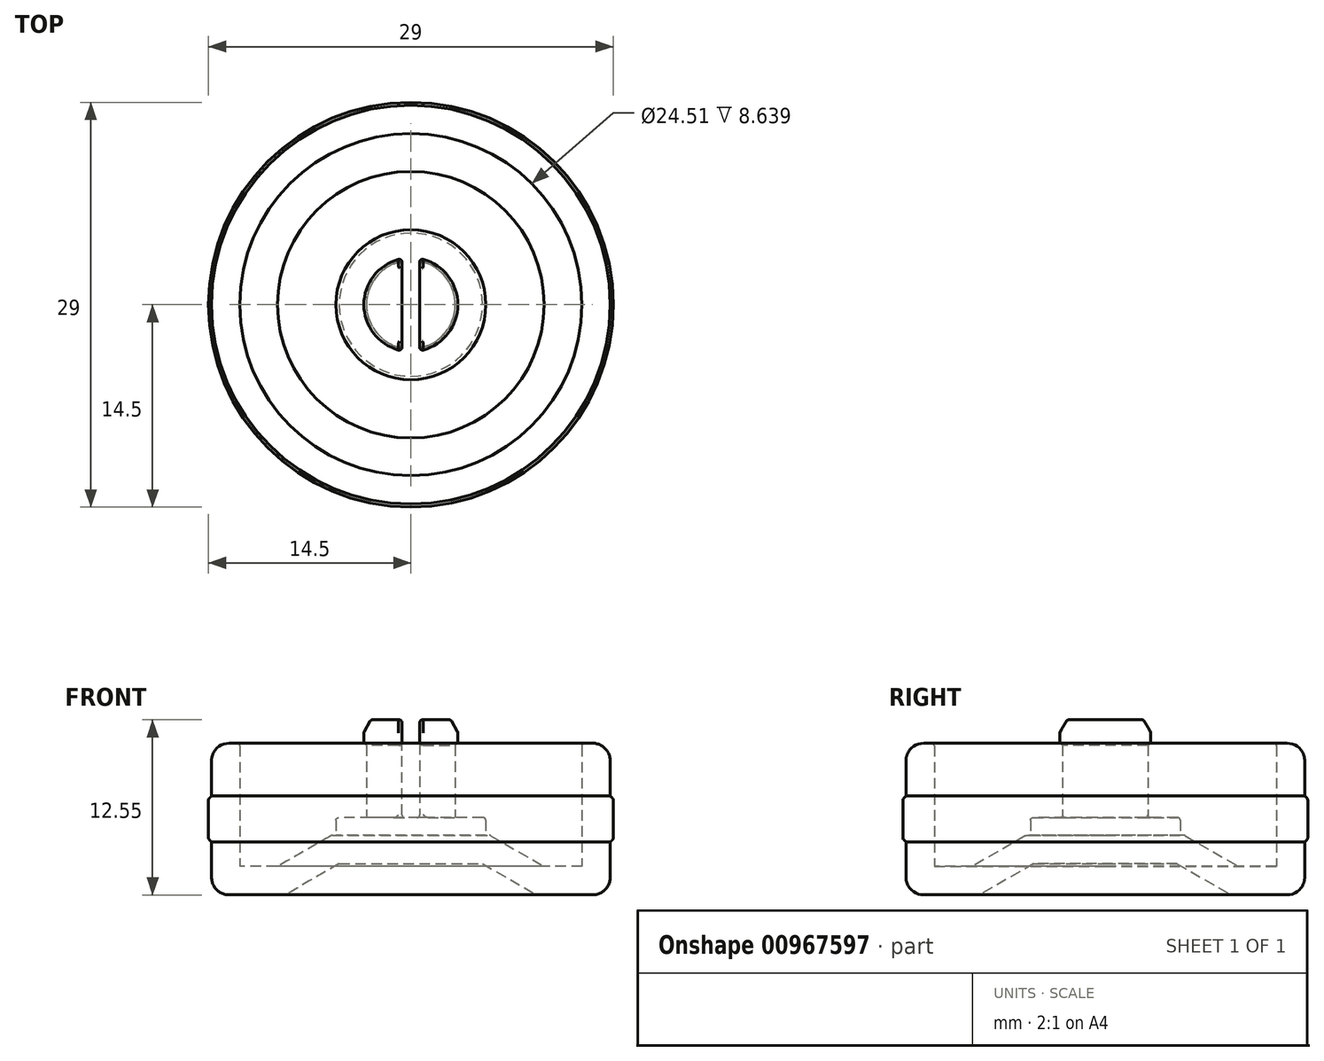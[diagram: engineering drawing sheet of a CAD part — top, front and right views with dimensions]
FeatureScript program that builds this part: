
annotation { "Feature Type Name" : "Feature", "Feature Type Description" : "" }
export const myFeature = defineFeature(function(context is Context, id is Id, definition is map)
    precondition{}
    {
        {
            var Q0;
            Q0=qCreatedBy(makeId("Top.planeOp"),FACE);
            var sketch = newSketch(context, id + "F0", { "sketchPlane" : qUnion([Q0])});
            skCircle(sketch, "E0", {"center": v(0, 0) * mm, "radius": 14.29 * mm});
            skSolve(sketch);
        }
        {
            var Q0;
            Q0 = qSketchRegion(id + "F0", true);
            extrude(context, id + "F1", {"entities" : qUnion([Q0]), "endBound" : BoundingType.SYMMETRIC, "depth" : 10.87 * mm, "offsetDistance" : 25.4 * mm});
        }
        {
            var Q0;
            Q0=qCreatedBy(makeId("Top.planeOp"),FACE);
            var sketch = newSketch(context, id + "F2", { "sketchPlane" : qUnion([Q0])});
            skCircle(sketch, "E1", {"center": v(0, 0) * mm, "radius": 14.5 * mm});
            skSolve(sketch);
        }
        {
            var Q0;
            Q0 = qSketchRegion(id + "F2", true);
            extrude(context, id + "F3", {"entities" : qUnion([Q0]), "operationType" : NewBodyOperationType.ADD, "endBound" : BoundingType.SYMMETRIC, "depth" : 3.38 * mm, "offsetDistance" : 25.4 * mm});
        }
        {
            var Q0;
            Q0=makeQuery(id+"F1.opExtrude","CAP_FACE",FACE,{"disambiguationData":[OSD([sQuery(id+"F0.wireOp",EDGE,"E0")])],"isStart":true});
            var sketch = newSketch(context, id + "F4", { "sketchPlane" : qUnion([Q0])});
            skCircle(sketch, "E2", {"center": v(0, 0) * mm, "radius": 9 * mm});
            skSolve(sketch);
        }
        {
            var Q0;
            Q0 = qSketchRegion(id + "F4", true);
            extrude(context, id + "F5", {"entities" : qUnion([Q0]), "operationType" : NewBodyOperationType.REMOVE, "oppositeDirection" : true, "depth" : 2.24 * mm, "offsetDistance" : 25.4 * mm});
        }
        {
            var Q0;
            Q0=makeQuery(id+"F5.boolean.opBoolean","COPY",EDGE,{"derivedFrom":makeQuery(id+"F5.opExtrude","CAP_EDGE",EDGE,{"disambiguationData":[OSD([sQuery(id+"F4.wireOp",EDGE,"E2")])],"isStart":false})});
            chamfer(context, id + "F6", {"entities" : qUnion([Q0]), "chamferType" : ChamferType.OFFSET_ANGLE, "width" : 2.24 * mm, "oppositeDirection" : true, "angle" : 60 * degree, "tangentPropagation" : true});
        }
        {
            var Q0;
            Q0=makeQuery(id+"F1.opExtrude","CAP_EDGE",EDGE,{"disambiguationData":[OSD([sQuery(id+"F0.wireOp",EDGE,"E0")])],"isStart":true});
            var Q1;
            Q1=makeQuery(id+"F1.opExtrude","CAP_EDGE",EDGE,{"disambiguationData":[OSD([sQuery(id+"F0.wireOp",EDGE,"E0")])],"isStart":false});
            fillet(context, id + "F7", {"entities" : qUnion([Q0, Q1]), "radius" : 1.27 * mm, "tangentPropagation" : true, "allowEdgeOverflow" : false});
        }
        {
            var Q0;
            Q0=makeQuery(id+"F1.opExtrude","CAP_FACE",FACE,{"disambiguationData":[OSD([sQuery(id+"F0.wireOp",EDGE,"E0")])],"isStart":false});
            shell(context, id + "F8", {"entities" : qUnion([Q0]), "thickness" : 2.03 * mm});
        }
        {
            var Q0;
            {var subQ0=sQuery(id+"F4.wireOp",EDGE,"E2");Q0=makeQuery(id+"F8.opShell","OFFSET_FACE",FACE,{"disambiguationData":[OSD([subQ0]),TDD([makeQuery(id+"F5.boolean.opBoolean","COPY",FACE,{"derivedFrom":makeQuery(id+"F5.opExtrude","CAP_FACE",FACE,{"disambiguationData":[OSD([subQ0])],"isStart":false})})])]});}
            var sketch = newSketch(context, id + "F9", { "sketchPlane" : qUnion([Q0])});
            skCircle(sketch, "E3", {"center": v(0, 0) * mm, "radius": 5.37 * mm});
            skSolve(sketch);
        }
        {
            var Q0;
            Q0 = qSketchRegion(id + "F9", true);
            extrude(context, id + "F10", {"entities" : qUnion([Q0]), "operationType" : NewBodyOperationType.ADD, "depth" : 1.27 * mm, "offsetDistance" : 25.4 * mm});
        }
        {
            var Q0;
            Q0=makeQuery(id+"F10.opExtrude","CAP_FACE",FACE,{"disambiguationData":[OSD([sQuery(id+"F9.wireOp",EDGE,"E3")])],"isStart":false});
            var sketch = newSketch(context, id + "F11", { "sketchPlane" : qUnion([Q0])});
            skCircle(sketch, "E4", {"center": v(0, 0) * mm, "radius": 3.18 * mm});
            skSolve(sketch);
        }
        {
            var Q0;
            Q0 = qSketchRegion(id + "F11", true);
            extrude(context, id + "F12", {"entities" : qUnion([Q0]), "operationType" : NewBodyOperationType.ADD, "depth" : 7 * mm, "offsetDistance" : 25.4 * mm});
        }
        {
            var Q0;
            Q0=makeQuery(id+"F12.opExtrude","CAP_FACE",FACE,{"disambiguationData":[OSD([sQuery(id+"F11.wireOp",EDGE,"E4")])],"isStart":false});
            var sketch = newSketch(context, id + "F13", { "sketchPlane" : qUnion([Q0])});
            skCircle(sketch, "E5", {"center": v(0, 0) * mm, "radius": 3.37 * mm});
            skSolve(sketch);
        }
        {
            var Q0;
            Q0 = qSketchRegion(id + "F13", true);
            extrude(context, id + "F14", {"entities" : qUnion([Q0]), "operationType" : NewBodyOperationType.ADD, "oppositeDirection" : true, "depth" : 1.9 * mm, "offsetDistance" : 25.4 * mm});
        }
        {
            var Q0;
            Q0=makeQuery(id+"F14.opExtrude","CAP_EDGE",EDGE,{"disambiguationData":[OSD([sQuery(id+"F13.wireOp",EDGE,"E5")])],"isStart":true});
            chamfer(context, id + "F15", {"entities" : qUnion([Q0]), "chamferType" : ChamferType.OFFSET_ANGLE, "width" : 0.5 * mm, "oppositeDirection" : false, "angle" : 60 * degree, "tangentPropagation" : true});
        }
        {
            var Q0;
            Q0=makeQuery(id+"F3.opExtrude","CAP_EDGE",EDGE,{"disambiguationData":[OSD([sQuery(id+"F2.wireOp",EDGE,"E1")])],"isStart":false});
            var Q1;
            Q1=makeQuery(id+"F3.opExtrude","CAP_EDGE",EDGE,{"disambiguationData":[OSD([sQuery(id+"F2.wireOp",EDGE,"E1")])],"isStart":true});
            chamfer(context, id + "F16", {"entities" : qUnion([Q0, Q1]), "width" : 0.25 * mm, "tangentPropagation" : true});
        }
        {
            var Q0;
            Q0=makeQuery(id+"F14.opExtrude","CAP_EDGE",EDGE,{"disambiguationData":[OSD([sQuery(id+"F13.wireOp",EDGE,"E5")])],"isStart":false});
            chamfer(context, id + "F17", {"entities" : qUnion([Q0]), "width" : 0.25 * mm, "tangentPropagation" : true});
        }
        {
            var Q0;
            Q0=makeQuery(id+"F14.boolean.opBoolean","MERGE",FACE,{"derivedFrom":[makeQuery(id+"F12.opExtrude","CAP_FACE",FACE,{"disambiguationData":[OSD([sQuery(id+"F11.wireOp",EDGE,"E4")])],"isStart":false}),makeQuery(id+"F14.opExtrude","CAP_FACE",FACE,{"disambiguationData":[OSD([sQuery(id+"F13.wireOp",EDGE,"E5")])],"isStart":true})]});
            var sketch = newSketch(context, id + "F18", { "sketchPlane" : qUnion([Q0])});
            skLineSegment(sketch, "E6", {"start": v(0, -3.37) * mm, "end": v(0, 3.37) * mm, "construction": true});
            skLineSegment(sketch, "E7.bottom", {"start": v(0.64, -3.37) * mm, "end": v(-0.64, -3.37) * mm});
            skLineSegment(sketch, "E7.top", {"start": v(0.64, 3.37) * mm, "end": v(-0.64, 3.37) * mm});
            skLineSegment(sketch, "E7.left", {"start": v(0.63, -3.37) * mm, "end": v(0.64, 3.37) * mm});
            skLineSegment(sketch, "E7.right", {"start": v(-0.64, -3.37) * mm, "end": v(-0.64, 3.37) * mm});
            skSolve(sketch);
        }
        {
            var Q0;
            Q0 = qSketchRegion(id + "F18", true);
            var Q1;
            Q1=makeQuery(id+"F10.opExtrude","CAP_FACE",FACE,{"disambiguationData":[OSD([sQuery(id+"F9.wireOp",EDGE,"E3")])],"isStart":false});
            extrude(context, id + "F19", {"entities" : qUnion([Q0]), "operationType" : NewBodyOperationType.REMOVE, "endBound" : BoundingType.UP_TO_SURFACE, "oppositeDirection" : true, "depth" : 25.4 * mm, "endBoundEntityFace" : qUnion([Q1]), "offsetDistance" : 25.4 * mm});
        }
        {
            var Q0;
            Q0=makeQuery(id+"F19.boolean.opBoolean","COPY",FACE,{"derivedFrom":makeQuery(id+"F19.opExtrude","SWEPT_FACE",FACE,{"disambiguationData":[OSD([sQuery(id+"F18.wireOp",EDGE,"E7.left")])]})});
            var Q1;
            Q1=makeQuery(id+"F19.boolean.opBoolean","COPY",FACE,{"derivedFrom":makeQuery(id+"F19.opExtrude","SWEPT_FACE",FACE,{"disambiguationData":[OSD([sQuery(id+"F18.wireOp",EDGE,"E7.right")])]})});
            var Q2;
            {var subQ0=makeQuery(id+"F12.opExtrude","CAP_FACE",FACE,{"disambiguationData":[OSD([sQuery(id+"F11.wireOp",EDGE,"E4")])],"isStart":false});var subQ1=sQuery(id+"F13.wireOp",EDGE,"E5");var subQ2=makeQuery(id+"F14.opExtrude","CAP_FACE",FACE,{"disambiguationData":[OSD([subQ1])],"isStart":true});Q2=makeQuery(id+"F19.boolean.opBoolean","SPLIT",EDGE,{"disambiguationData":[TD([makeQuery(id+"F19.opExtrude","SWEPT_FACE",FACE,{"disambiguationData":[OSD([sQuery(id+"F18.wireOp",EDGE,"E7.right")])]})])],"derivedFrom":makeQuery(id+"F15.opChamfer","BLEND_EDGE",EDGE,{"blendedFrom":[makeQuery(id+"F14.opExtrude","CAP_EDGE",EDGE,{"disambiguationData":[OSD([subQ1])],"isStart":true}),makeQuery(id+"F14.boolean.opBoolean","MERGE",FACE,{"derivedFrom":[subQ0,subQ2]})],"blendedInto":[makeQuery(id+"F14.boolean.opBoolean","MERGE",FACE,{"derivedFrom":[subQ0,subQ2]})]})});}
            var Q3;
            {var subQ0=sQuery(id+"F13.wireOp",EDGE,"E5");var subQ1=makeQuery(id+"F14.opExtrude","SWEPT_FACE",FACE,{"disambiguationData":[OSD([subQ0])]});Q3=makeQuery(id+"F19.boolean.opBoolean","SPLIT",EDGE,{"disambiguationData":[TD([makeQuery(id+"F19.opExtrude","SWEPT_FACE",FACE,{"disambiguationData":[OSD([sQuery(id+"F18.wireOp",EDGE,"E7.right")])]})])],"derivedFrom":makeQuery(id+"F15.opChamfer","BLEND_EDGE",EDGE,{"blendedFrom":[makeQuery(id+"F14.opExtrude","CAP_EDGE",EDGE,{"disambiguationData":[OSD([subQ0])],"isStart":true}),subQ1],"blendedInto":[subQ1]})});}
            var Q4;
            {var subQ0=sQuery(id+"F13.wireOp",EDGE,"E5");var subQ1=makeQuery(id+"F14.opExtrude","SWEPT_FACE",FACE,{"disambiguationData":[OSD([subQ0])]});Q4=makeQuery(id+"F19.boolean.opBoolean","SPLIT",EDGE,{"disambiguationData":[TD([makeQuery(id+"F19.opExtrude","SWEPT_FACE",FACE,{"disambiguationData":[OSD([sQuery(id+"F18.wireOp",EDGE,"E7.right")])]})])],"derivedFrom":makeQuery(id+"F17.opChamfer","BLEND_EDGE",EDGE,{"blendedFrom":[makeQuery(id+"F14.opExtrude","CAP_EDGE",EDGE,{"disambiguationData":[OSD([subQ0])],"isStart":false}),subQ1],"blendedInto":[subQ1]})});}
            var Q5;
            {var subQ0=makeQuery(id+"F12.opExtrude","CAP_FACE",FACE,{"disambiguationData":[OSD([sQuery(id+"F11.wireOp",EDGE,"E4")])],"isStart":false});var subQ1=sQuery(id+"F13.wireOp",EDGE,"E5");var subQ2=makeQuery(id+"F14.opExtrude","CAP_FACE",FACE,{"disambiguationData":[OSD([subQ1])],"isStart":true});Q5=makeQuery(id+"F19.boolean.opBoolean","SPLIT",EDGE,{"disambiguationData":[TD([makeQuery(id+"F19.opExtrude","SWEPT_FACE",FACE,{"disambiguationData":[OSD([sQuery(id+"F18.wireOp",EDGE,"E7.left")])]})])],"derivedFrom":makeQuery(id+"F15.opChamfer","BLEND_EDGE",EDGE,{"blendedFrom":[makeQuery(id+"F14.opExtrude","CAP_EDGE",EDGE,{"disambiguationData":[OSD([subQ1])],"isStart":true}),makeQuery(id+"F14.boolean.opBoolean","MERGE",FACE,{"derivedFrom":[subQ0,subQ2]})],"blendedInto":[makeQuery(id+"F14.boolean.opBoolean","MERGE",FACE,{"derivedFrom":[subQ0,subQ2]})]})});}
            var Q6;
            {var subQ0=sQuery(id+"F13.wireOp",EDGE,"E5");var subQ1=makeQuery(id+"F14.opExtrude","SWEPT_FACE",FACE,{"disambiguationData":[OSD([subQ0])]});Q6=makeQuery(id+"F19.boolean.opBoolean","SPLIT",EDGE,{"disambiguationData":[TD([makeQuery(id+"F19.opExtrude","SWEPT_FACE",FACE,{"disambiguationData":[OSD([sQuery(id+"F18.wireOp",EDGE,"E7.left")])]})])],"derivedFrom":makeQuery(id+"F15.opChamfer","BLEND_EDGE",EDGE,{"blendedFrom":[makeQuery(id+"F14.opExtrude","CAP_EDGE",EDGE,{"disambiguationData":[OSD([subQ0])],"isStart":true}),subQ1],"blendedInto":[subQ1]})});}
            var Q7;
            {var subQ0=sQuery(id+"F13.wireOp",EDGE,"E5");var subQ1=makeQuery(id+"F14.opExtrude","SWEPT_FACE",FACE,{"disambiguationData":[OSD([subQ0])]});Q7=makeQuery(id+"F19.boolean.opBoolean","SPLIT",EDGE,{"disambiguationData":[TD([makeQuery(id+"F19.opExtrude","SWEPT_FACE",FACE,{"disambiguationData":[OSD([sQuery(id+"F18.wireOp",EDGE,"E7.left")])]})])],"derivedFrom":makeQuery(id+"F17.opChamfer","BLEND_EDGE",EDGE,{"blendedFrom":[makeQuery(id+"F14.opExtrude","CAP_EDGE",EDGE,{"disambiguationData":[OSD([subQ0])],"isStart":false}),subQ1],"blendedInto":[subQ1]})});}
            var Q8;
            {var subQ0=sQuery(id+"F0.wireOp",EDGE,"E0");var subQ1=makeQuery(id+"F1.opExtrude","CAP_FACE",FACE,{"disambiguationData":[OSD([subQ0])],"isStart":false});var subQ2=makeQuery(id+"F1.opExtrude","CAP_EDGE",EDGE,{"disambiguationData":[OSD([subQ0])],"isStart":false});Q8=makeQuery(id+"F8.opShell","OFFSET_EDGE",EDGE,{"disambiguationData":[OSD([subQ0]),TDD([makeQuery(id+"F7.opFillet","BLEND_EDGE",EDGE,{"blendedFrom":[subQ2,subQ1],"blendedInto":[subQ1]}),makeQuery(id+"F7.opFillet","BLEND_EDGE",EDGE,{"blendedFrom":[subQ2,makeQuery(id+"F3.boolean.opBoolean","SPLIT",FACE,{"disambiguationData":[TD([subQ1])],"derivedFrom":makeQuery(id+"F1.opExtrude","SWEPT_FACE",FACE,{"disambiguationData":[OSD([subQ0])]})})],"blendedInto":[makeQuery(id+"F3.boolean.opBoolean","SPLIT",FACE,{"disambiguationData":[TD([subQ1])],"derivedFrom":makeQuery(id+"F1.opExtrude","SWEPT_FACE",FACE,{"disambiguationData":[OSD([subQ0])]})})]})])]});}
            var Q9;
            Q9=makeQuery(id+"F6.opChamfer","BLEND_EDGE",EDGE,{"blendedFrom":[makeQuery(id+"F5.boolean.opBoolean","COPY",EDGE,{"derivedFrom":makeQuery(id+"F5.opExtrude","CAP_EDGE",EDGE,{"disambiguationData":[OSD([sQuery(id+"F4.wireOp",EDGE,"E2")])],"isStart":false})}),makeQuery(id+"F1.opExtrude","CAP_FACE",FACE,{"disambiguationData":[OSD([sQuery(id+"F0.wireOp",EDGE,"E0")])],"isStart":true})],"blendedInto":[makeQuery(id+"F1.opExtrude","CAP_FACE",FACE,{"disambiguationData":[OSD([sQuery(id+"F0.wireOp",EDGE,"E0")])],"isStart":true})]});
            var Q10;
            Q10=makeQuery(id+"F10.opExtrude","CAP_EDGE",EDGE,{"disambiguationData":[OSD([sQuery(id+"F9.wireOp",EDGE,"E3")])],"isStart":false});
            var Q11;
            Q11=makeQuery(id+"F8.opShell","OFFSET_EDGE",EDGE,{"disambiguationData":[OSD([sQuery(id+"F4.wireOp",EDGE,"E2")])]});
            var Q12;
            {var subQ0=sQuery(id+"F2.wireOp",EDGE,"E1");Q12=makeQuery(id+"F16.opChamfer","BLEND_EDGE",EDGE,{"blendedFrom":[makeQuery(id+"F3.opExtrude","CAP_EDGE",EDGE,{"disambiguationData":[OSD([subQ0])],"isStart":false}),makeQuery(id+"F3.opExtrude","SWEPT_FACE",FACE,{"disambiguationData":[OSD([subQ0])]})],"blendedInto":[makeQuery(id+"F3.opExtrude","SWEPT_FACE",FACE,{"disambiguationData":[OSD([subQ0])]})]});}
            var Q13;
            {var subQ0=sQuery(id+"F2.wireOp",EDGE,"E1");Q13=makeQuery(id+"F16.opChamfer","BLEND_EDGE",EDGE,{"blendedFrom":[makeQuery(id+"F3.opExtrude","CAP_EDGE",EDGE,{"disambiguationData":[OSD([subQ0])],"isStart":true}),makeQuery(id+"F3.opExtrude","SWEPT_FACE",FACE,{"disambiguationData":[OSD([subQ0])]})],"blendedInto":[makeQuery(id+"F3.opExtrude","SWEPT_FACE",FACE,{"disambiguationData":[OSD([subQ0])]})]});}
            fillet(context, id + "F20", {"entities" : qUnion([Q0, Q1, Q2, Q3, Q4, Q5, Q6, Q7, Q8, Q9, Q10, Q11, Q12, Q13]), "radius" : .2 * mm, "tangentPropagation" : true, "allowEdgeOverflow" : false});
        }
    });
